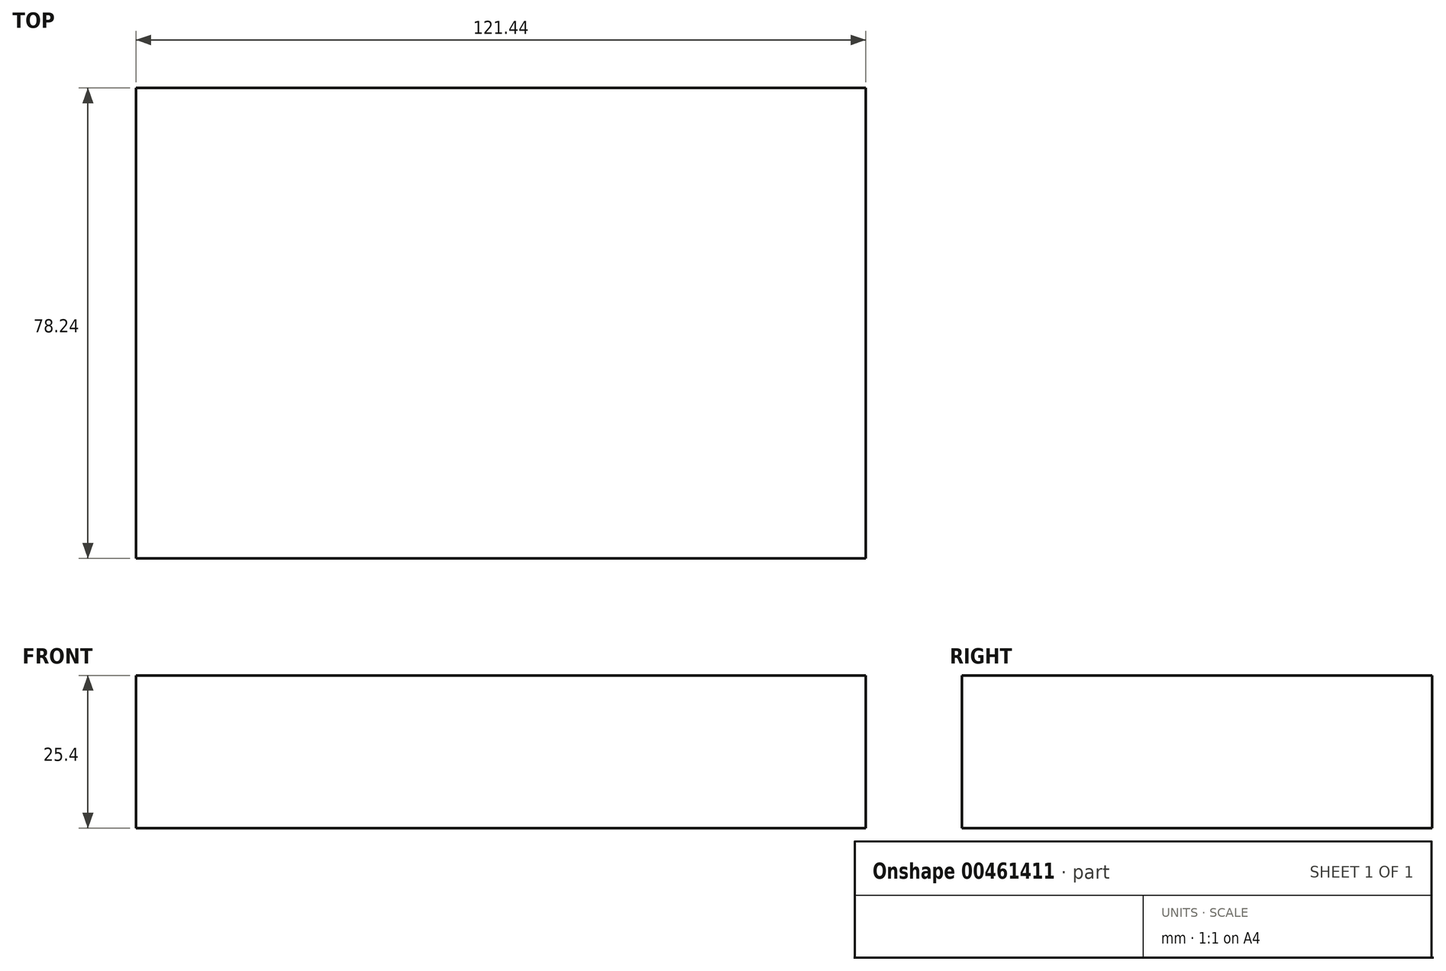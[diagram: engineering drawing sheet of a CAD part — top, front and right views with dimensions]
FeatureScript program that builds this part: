
annotation { "Feature Type Name" : "Feature", "Feature Type Description" : "" }
export const myFeature = defineFeature(function(context is Context, id is Id, definition is map)
    precondition{}
    {
        {
            var Q0;
            Q0=qCreatedBy(makeId("Top.planeOp"),FACE);
            var sketch = newSketch(context, id + "F0", { "sketchPlane" : qUnion([Q0])});
            skLineSegment(sketch, "E0.bottom", {"start": v(-59.67, 40.52) * mm, "end": v(61.77, 40.52) * mm});
            skLineSegment(sketch, "E0.top", {"start": v(-59.67, -37.72) * mm, "end": v(61.77, -37.72) * mm});
            skLineSegment(sketch, "E0.left", {"start": v(-59.67, 40.52) * mm, "end": v(-59.67, -37.72) * mm});
            skLineSegment(sketch, "E0.right", {"start": v(61.77, 40.52) * mm, "end": v(61.77, -37.72) * mm});
            skSolve(sketch);
        }
        {
            var Q0;
            Q0=makeQuery(id+"F0.imprint","IMPRINT",FACE,{"disambiguationData":[TD([[makeQuery(id+"F0.imprint","IMPRINT",EDGE,{"derivedFrom":sQuery(id+"F0.wireOp",EDGE,"E0.bottom")}),-1.0]])]});
            extrude(context, id + "F1", {"entities" : qUnion([Q0]), "depth" : 25.4 * mm});
        }
    });
